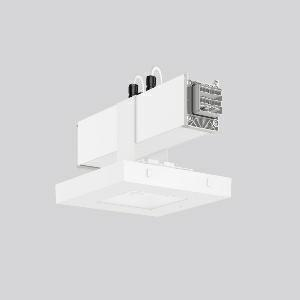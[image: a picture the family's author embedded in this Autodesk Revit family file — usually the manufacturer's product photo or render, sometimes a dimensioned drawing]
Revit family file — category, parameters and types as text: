
# Revit family: linedo_module_rt_9503rt_762_437_000_903a
name_source: partatom
category: Lighting Fixtures
units: mm (PartAtom-declared; Revit-internal decimal feet)

## family parameters
Cut with Voids When Loaded = No
Host = Face
Light Source = No
Part Type = Normal
Room Calculation Point = No
Round Connector Dimension = Use Diameter
Shared = No

## types (1)
- LINEDO Module RT (1 x LED Modul 765, 370 lm, 6500)
    Apparent Load = 7 VA
    CIE Flux Codes = 91 98 100 100 100
    Color Rendering = 70
    Color Temperature = 6500
    Default Elevation = 1800 mm
    Description = LINEDO, 6,7 W, 370 lm, 765, white, on/off
Continuous line luminaire, L 330 B 198 H 170, SBS, 3 h, emergency-340 lm, DALI-Sibe
    Height = 170 mm  [stored 0.557743 ft]
    Lamp = 1 x LED Modul 765
    Lamp Light Flux = 370 lm
    Lamp count = 1
    Length = 330 mm
    Lifetime = 50000 h
    Luminous efficacy = 55 lm/W
    Manufacturer = RZB
    ModVariant = No
    Model = 9503RT.762.437.000
    Mounting Place = Ceiling
    Mounting Type = Pendant, Surface mounted
    Number of Poles = 1
    OnlyDefault = Yes
    Power Factor = 1
    Product Name = LINEDO Module RT
    Product group = Surface mounted continuous line luminaire system
    ProductGroupID = 310
    Protection Class = Protection class I
    Protection Degree = IP 54
    RLX_Detail_Level = 1
    RLX_Emergency_Light_Flux = 340 lm
    RLX_Emergency_Type = 3
    RLX_Emergency_Type_DB = Yes
    RlxData = <blob elided: 20229 chars, md5=99404048>
    Socket = socket
    Standby Power = 0 W
    System Light Flux = 370 lm
    System Power = 7 W
    Type Comments = Product without accessories
    Type Image = 9503rw.762.434.000.jpg
    URL = http://relux.com
    VarID = ---
    Voltage = 230 V
    Voltage Range = 220-240 V
    Weight = 0.00 kg
    Width = 198 mm

note: [stored X ft] marks values corroborated as IEEE doubles in the binary element streams (Revit-internal decimal feet)

## geometry (parser evidence)
native form markers: Blend x4, Sweep x12
no freeform markers — native parametric forms only
